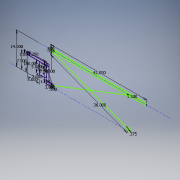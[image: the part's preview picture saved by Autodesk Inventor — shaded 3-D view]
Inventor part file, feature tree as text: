
AUTODESK INVENTOR PART (.ipt)
format: ipt  version: 2017 SP1 (Build 210196100, 196)  size: 120,320 bytes
history: native  units: in
note: dims shown in document units (in); Inventor stores cm internally (conversion verified against a paired STEP export)
features: sketch x1
ambient origin geometry x8: Origin, YZ Plane, XZ Plane, XY Plane, X Axis, Y Axis, Z Axis, Center Point
feature tree (1):
  sketch  "Sketch1"  dims[d0=5.0in d1=2.0in d3=1.0in d4=5.0in d5=7.5in d7=8.25in d10=1.25in d11=3.25in d12=1.0in d13=42.0in d15=0.375in d16=14.0in d17=0.125in d18=1.5in d19=3.0in d21=8.0in d22=0.0in d23=36.0in d24=0.5in d25=0.125in d26=0.5in d27=0.75in d28=1.25in]
